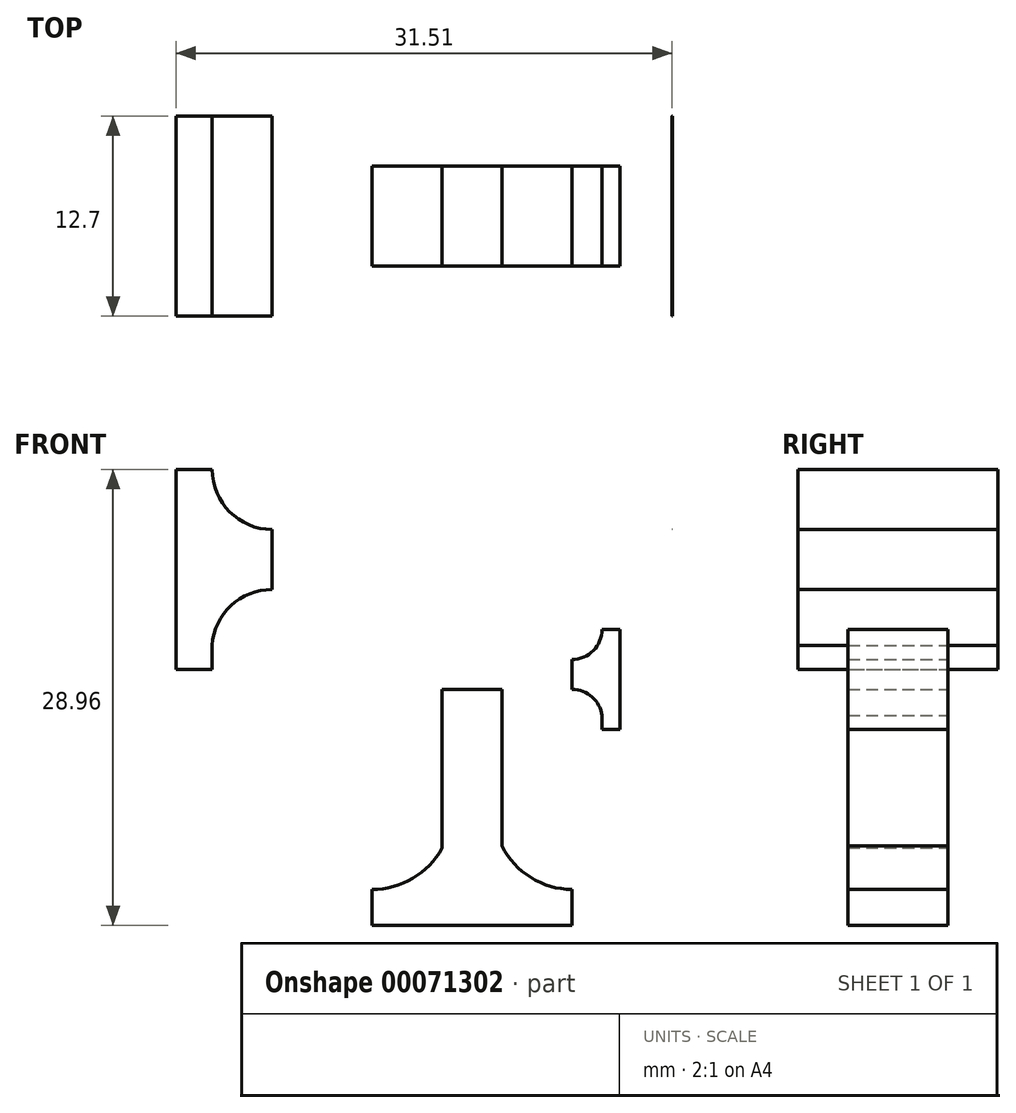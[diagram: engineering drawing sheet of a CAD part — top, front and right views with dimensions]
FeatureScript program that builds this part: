
annotation { "Feature Type Name" : "Feature", "Feature Type Description" : "" }
export const myFeature = defineFeature(function(context is Context, id is Id, definition is map)
    precondition{}
    {
        {
            var Q0;
            Q0=qCreatedBy(makeId("Front.planeOp"),FACE);
            var sketch = newSketch(context, id + "F0", { "sketchPlane" : qUnion([Q0])});
            skLineSegment(sketch, "E0.rect.bottom", {"start": v(3.81, -12.7) * mm, "end": v(-3.81, -12.7) * mm});
            skLineSegment(sketch, "E0.rect.top", {"start": v(3.8, 12.7) * mm, "end": v(-3.81, 12.7) * mm});
            skLineSegment(sketch, "E0.rect.left", {"start": v(3.8, -12.7) * mm, "end": v(3.8, 12.7) * mm});
            skLineSegment(sketch, "E0.rect.right", {"start": v(-3.81, -12.7) * mm, "end": v(-3.81, 12.7) * mm});
            skPoint(sketch, "E0.rect.middle", {"position": v(0, 0) * mm});
            skLineSegment(sketch, "E1.bottom", {"start": v(-16.51, 12.7) * mm, "end": v(16.5, 12.7) * mm});
            skLineSegment(sketch, "E1.top", {"start": v(-16.51, 16.51) * mm, "end": v(16.51, 16.51) * mm});
            skLineSegment(sketch, "E1.left", {"start": v(-16.51, 12.7) * mm, "end": v(-16.51, 16.51) * mm});
            skLineSegment(sketch, "E1.right", {"start": v(16.5, 12.7) * mm, "end": v(16.5, 16.51) * mm});
            skLineSegment(sketch, "E2.bottom", {"start": v(16.51, 20.32) * mm, "end": v(18.8, 20.32) * mm});
            skLineSegment(sketch, "E2.top", {"start": v(16.5, 7.62) * mm, "end": v(18.8, 7.62) * mm});
            skLineSegment(sketch, "E2.left", {"start": v(16.5, 20.32) * mm, "end": v(16.5, 7.62) * mm});
            skLineSegment(sketch, "E2.right", {"start": v(18.8, 20.32) * mm, "end": v(18.8, 7.62) * mm});
            skLineSegment(sketch, "E3.bottom", {"start": v(-16.51, 20.32) * mm, "end": v(-18.8, 20.32) * mm});
            skLineSegment(sketch, "E3.top", {"start": v(-16.5, 7.62) * mm, "end": v(-18.8, 7.62) * mm});
            skLineSegment(sketch, "E3.left", {"start": v(-16.51, 20.32) * mm, "end": v(-16.51, 7.62) * mm});
            skLineSegment(sketch, "E3.right", {"start": v(-18.8, 20.32) * mm, "end": v(-18.8, 7.62) * mm});
            skLineSegment(sketch, "E4.bottom", {"start": v(-12.7, -12.7) * mm, "end": v(12.7, -12.7) * mm});
            skLineSegment(sketch, "E4.top", {"start": v(-12.7, -17.27) * mm, "end": v(12.7, -17.27) * mm});
            skLineSegment(sketch, "E4.left", {"start": v(-12.7, -12.7) * mm, "end": v(-12.7, -17.27) * mm});
            skLineSegment(sketch, "E4.right", {"start": v(12.7, -12.7) * mm, "end": v(12.7, -17.27) * mm});
            skArc(sketch, "E5", {"start": v(-16.51, 20.32) * mm, "mid": v(-15.4, 17.63) * mm, "end": v(-12.7, 16.51) * mm});
            skArc(sketch, "E6", {"start": v(12.7, 16.51) * mm, "mid": v(15.4, 17.63) * mm, "end": v(16.5, 20.32) * mm});
            skArc(sketch, "E7", {"start": v(-12.7, 12.7) * mm, "mid": v(-15.31, 11.67) * mm, "end": v(-16.51, 9.14) * mm});
            skArc(sketch, "E8", {"start": v(16.5, 9.38) * mm, "mid": v(15.24, 11.76) * mm, "end": v(12.72, 12.7) * mm});
            skArc(sketch, "E9", {"start": v(-12.7, -12.7) * mm, "mid": v(-7.54, -11.3) * mm, "end": v(-3.8, -7.46) * mm});
            skLineSegment(sketch, "E10", {"start": v(-12.7, 26.78) * mm, "end": v(-12.7, 5.25) * mm});
            skLineSegment(sketch, "E11", {"start": v(12.7, 23.9) * mm, "end": v(12.73, 5.76) * mm});
            skArc(sketch, "E12", {"start": v(3.8, -7.16) * mm, "mid": v(7.46, -11.2) * mm, "end": v(12.7, -12.7) * mm});
            skSolve(sketch);
        }
        {
            var Q0;
            {var subQ3=sQuery(id+"F0.wireOp",EDGE,"d77c4c86-c386-4595-a15e-4eeda52f04e1");Q0=makeQuery(id+"F0.imprint","IMPRINT",FACE,{"disambiguationData":[TD([[makeQuery(id+"F0.imprint","IMPRINT",EDGE,{"derivedFrom":subQ3}),-1.0]])]});}
            var Q1;
            {var subQ3=sQuery(id+"F0.wireOp",EDGE,"E9");Q1=makeQuery(id+"F0.imprint","IMPRINT",FACE,{"disambiguationData":[TD([[makeQuery(id+"F0.imprint","IMPRINT",EDGE,{"derivedFrom":subQ3}),-1.0]])]});}
            var Q2;
            {var subQ0=sQuery(id+"F0.wireOp",EDGE,"E3.left");var subQ1=sQuery(id+"F0.wireOp",EDGE,"E1.bottom");var subQ2=makeQuery(id+"F0.imprint","INTERSECT",VERTEX,{"derivedFrom":[subQ1,subQ0]});Q2=makeQuery(id+"F0.imprint","IMPRINT",FACE,{"disambiguationData":[TD([[makeQuery(id+"F0.imprint","IMPRINT",EDGE,{"disambiguationData":[TD([[subQ2,-1.0]])],"derivedFrom":subQ1}),-1.0]])]});}
            var Q3;
            {var subQ0=sQuery(id+"F0.wireOp",EDGE,"E2.left");var subQ1=sQuery(id+"F0.wireOp",EDGE,"E1.bottom");var subQ2=makeQuery(id+"F0.imprint","INTERSECT",VERTEX,{"derivedFrom":[subQ1,subQ0]});Q3=makeQuery(id+"F0.imprint","IMPRINT",FACE,{"disambiguationData":[TD([[makeQuery(id+"F0.imprint","IMPRINT",EDGE,{"disambiguationData":[TD([[subQ2,1.0]])],"derivedFrom":subQ1}),-1.0]])]});}
            var Q4;
            {var subQ3=sQuery(id+"F0.wireOp",EDGE,"E5");Q4=makeQuery(id+"F0.imprint","IMPRINT",FACE,{"disambiguationData":[TD([[makeQuery(id+"F0.imprint","IMPRINT",EDGE,{"derivedFrom":subQ3}),-1.0]])]});}
            var Q5;
            {var subQ3=sQuery(id+"F0.wireOp",EDGE,"E6");Q5=makeQuery(id+"F0.imprint","IMPRINT",FACE,{"disambiguationData":[TD([[makeQuery(id+"F0.imprint","IMPRINT",EDGE,{"derivedFrom":subQ3}),-1.0]])]});}
            var Q6;
            {var subQ3=sQuery(id+"F0.wireOp",EDGE,"E2.bottom");Q6=makeQuery(id+"F0.imprint","IMPRINT",FACE,{"disambiguationData":[TD([[makeQuery(id+"F0.imprint","IMPRINT",EDGE,{"derivedFrom":subQ3}),-1.0]])]});}
            var Q7;
            {var subQ3=sQuery(id+"F0.wireOp",EDGE,"E3.bottom");Q7=makeQuery(id+"F0.imprint","IMPRINT",FACE,{"disambiguationData":[TD([[makeQuery(id+"F0.imprint","IMPRINT",EDGE,{"derivedFrom":subQ3}),1.0]])]});}
            var Q8;
            Q8=makeQuery(id+"F0.imprint","IMPRINT",FACE,{"disambiguationData":[TD([[makeQuery(id+"F0.imprint","IMPRINT",EDGE,{"derivedFrom":sQuery(id+"F0.wireOp",EDGE,"E4.top")}),1.0]])]});
            var Q9;
            {var subQ4=sQuery(id+"F0.wireOp",EDGE,"E4.bottom");var subQ6=sQuery(id+"F0.wireOp",EDGE,"E0.rect.left");var subQ7=makeQuery(id+"F0.imprint","INTERSECT",VERTEX,{"derivedFrom":[subQ6,subQ4]});Q9=makeQuery(id+"F0.imprint","IMPRINT",FACE,{"disambiguationData":[TD([[makeQuery(id+"F0.imprint","IMPRINT",EDGE,{"disambiguationData":[TD([[subQ7,-1.0]])],"derivedFrom":subQ6}),1.0]])]});}
            var Q10;
            {var subQ3=sQuery(id+"F0.wireOp",EDGE,"E3.left");var subQ6=sQuery(id+"F0.wireOp",EDGE,"E1.bottom");var subQ11=makeQuery(id+"F0.imprint","INTERSECT",VERTEX,{"derivedFrom":[subQ6,subQ3]});Q10=makeQuery(id+"F0.imprint","IMPRINT",FACE,{"disambiguationData":[TD([[makeQuery(id+"F0.imprint","IMPRINT",EDGE,{"disambiguationData":[TD([[subQ11,-1.0]])],"derivedFrom":subQ6}),1.0]])]});}
            var Q11;
            {var subQ0=sQuery(id+"F0.wireOp",EDGE,"E7");var subQ1=sQuery(id+"F0.wireOp",EDGE,"E1.bottom");var subQ2=makeQuery(id+"F0.imprint","INTERSECT",VERTEX,{"disambiguationData":[OD(0.0)],"derivedFrom":[subQ1,subQ0]});Q11=makeQuery(id+"F0.imprint","IMPRINT",FACE,{"disambiguationData":[TD([[makeQuery(id+"F0.imprint","IMPRINT",EDGE,{"disambiguationData":[TD([[subQ2,1.0]])],"derivedFrom":subQ1}),1.0]])]});}
            var Q12;
            {var subQ0=sQuery(id+"F0.wireOp",EDGE,"E8");var subQ1=sQuery(id+"F0.wireOp",EDGE,"E1.bottom");var subQ2=makeQuery(id+"F0.imprint","INTERSECT",VERTEX,{"disambiguationData":[OD(0.0)],"derivedFrom":[subQ1,subQ0]});Q12=makeQuery(id+"F0.imprint","IMPRINT",FACE,{"disambiguationData":[TD([[makeQuery(id+"F0.imprint","IMPRINT",EDGE,{"disambiguationData":[TD([[subQ2,-1.0]])],"derivedFrom":subQ1}),1.0]])]});}
            var Q13;
            {var subQ4=sQuery(id+"F0.wireOp",EDGE,"E1.bottom");var subQ5=makeQuery(id+"F0.imprint","INTERSECT",VERTEX,{"derivedFrom":[sQuery(id+"F0.wireOp",EDGE,"E0.rect.left"),subQ4]});Q13=makeQuery(id+"F0.imprint","IMPRINT",FACE,{"disambiguationData":[TD([[makeQuery(id+"F0.imprint","IMPRINT",EDGE,{"disambiguationData":[TD([[subQ5,1.0]])],"derivedFrom":subQ4}),1.0]])]});}
            var Q14;
            {var subQ0=sQuery(id+"F0.wireOp",EDGE,"E2.left");var subQ1=sQuery(id+"F0.wireOp",EDGE,"E1.top");var subQ2=makeQuery(id+"F0.imprint","INTERSECT",VERTEX,{"derivedFrom":[subQ1,subQ0]});Q14=makeQuery(id+"F0.imprint","IMPRINT",FACE,{"disambiguationData":[TD([[makeQuery(id+"F0.imprint","IMPRINT",EDGE,{"disambiguationData":[TD([[subQ2,1.0]])],"derivedFrom":subQ1}),1.0]])]});}
            var Q15;
            {var subQ3=sQuery(id+"F0.wireOp",EDGE,"E12");Q15=makeQuery(id+"F0.imprint","IMPRINT",FACE,{"disambiguationData":[TD([[makeQuery(id+"F0.imprint","IMPRINT",EDGE,{"derivedFrom":subQ3}),-1.0]])]});}
            extrude(context, id + "F1", {"entities" : qUnion([Q0, Q1, Q2, Q3, Q4, Q5, Q6, Q7, Q8, Q9, Q10, Q11, Q12, Q13, Q14, Q15]), "endBound" : BoundingType.SYMMETRIC, "depth" : 12.7 * mm});
        }
        {
            var Q0;
            Q0=makeQuery(id+"F1.opExtrude","SWEPT_BODY",BODY,{"disambiguationData":[OSD([sQuery(id+"F0.wireOp",EDGE,"E0.rect.left"),sQuery(id+"F0.wireOp",EDGE,"E0.rect.right"),sQuery(id+"F0.wireOp",EDGE,"E1.bottom"),sQuery(id+"F0.wireOp",EDGE,"E1.top"),sQuery(id+"F0.wireOp",EDGE,"E2.bottom"),sQuery(id+"F0.wireOp",EDGE,"E2.top"),sQuery(id+"F0.wireOp",EDGE,"E2.left"),sQuery(id+"F0.wireOp",EDGE,"E2.right"),sQuery(id+"F0.wireOp",EDGE,"E3.bottom"),sQuery(id+"F0.wireOp",EDGE,"E3.top"),sQuery(id+"F0.wireOp",EDGE,"E3.left"),sQuery(id+"F0.wireOp",EDGE,"E3.right"),sQuery(id+"F0.wireOp",EDGE,"E4.top"),sQuery(id+"F0.wireOp",EDGE,"E4.left"),sQuery(id+"F0.wireOp",EDGE,"E4.right"),sQuery(id+"F0.wireOp",EDGE,"E5"),sQuery(id+"F0.wireOp",EDGE,"E6"),sQuery(id+"F0.wireOp",EDGE,"E7"),sQuery(id+"F0.wireOp",EDGE,"E8"),sQuery(id+"F0.wireOp",EDGE,"E9"),sQuery(id+"F0.wireOp",EDGE,"E12")])]});
            var Q1;
            Q1=qCreatedBy(makeId("Origin.pointOp"),VERTEX);
            transform(context, id + "F2", {"entities" : qUnion([Q0]), "transformType" : TransformType.SCALE_UNIFORMLY, "scale" : 0.5, "scalePoint" : qUnion([Q1]), "makeCopy" : false});
        }
    });
